# Revit family: CADS_Vent-Axia_MechEquip_Fan_SDX_InlineEC - EXTRACT
name_source: partatom
category: Mechanical Equipment
units: mm (PartAtom-declared; Revit-internal decimal feet)

## family parameters
Always vertical = Yes
Cut with Voids When Loaded = No
OmniClass Number = 23.75.00.00
OmniClass Title = Climate Control (HVAC)
Part Type = Normal
Room Calculation Point = No
Round Connector Dimension = Use Diameter
Shared = No
Work Plane-Based = No

## types (5) — shared parameters
AirflowRateRange = 0.0 L/s
AssemblyPlace = UNKNOWN
AssetType = FIXED
B = 175 mm  [stored 0.574147 ft]
DurationUnit = Year
ExteriorInsulation = No
Fitting Type = Ignore
GrossWeight = 0.00 kg
HasProtectiveEarth = No
IfcExportAs = IfcFanType
IsExtendedWarranty = No
ManufacturerAddress = Fleming Way
Crawley 
RH10 9YX
Quantity = 1
RatedCurrent = 0 A
RatedVoltage = 0 V
Status = New
WarrantyGuarantor = Vent-Axia Limited
WorkingPressure = 0.0 Pa
zero-valued in all types: CADS_Index, CADS_Usage, Default Elevation, ExpectedServiceLife, NumberOfPoles

## per-type parameters (varying)
| type | ModelReference | NominalDiameter | NominalHeight | NominalLength | NominalWidth |
| SDX125EC | INLINE 125mm FAN - EC MOTOR | 125 mm  [stored 0.410105 ft] | 245 mm  [stored 0.803806 ft] | 207 mm  [stored 0.679134 ft] | 245 mm  [stored 0.803806 ft] |
| SDX150EC | INLINE 150mm FAN - EC MOTOR | 150 mm | 344 mm  [stored 1.12861 ft] | 222 mm | 344 mm  [stored 1.12861 ft] |
| SDX200EC | INLINE 200mm FAN - EC MOTOR | 200 mm  [stored 0.656168 ft] | 345 mm  [stored 1.13189 ft] | 240 mm  [stored 0.787402 ft] | 345 mm  [stored 1.13189 ft] |
| SDX250EC | INLINE 250mm FAN - EC MOTOR | 250 mm  [stored 0.82021 ft] | 345 mm  [stored 1.13189 ft] | 245 mm  [stored 0.803806 ft] | 345 mm  [stored 1.13189 ft] |
| SDX315EC | INLINE 315mm FAN - EC MOTOR | 315 mm  [stored 1.03346 ft] | 400 mm  [stored 1.31234 ft] | 250 mm  [stored 0.82021 ft] | 400 mm  [stored 1.31234 ft] |

note: column(s) folded — value = type name in every type: ModelNumber

note: [stored X ft] marks values corroborated as IEEE doubles in the binary element streams (Revit-internal decimal feet)

## geometry (parser evidence)
native form markers: Sweep x5
no freeform markers — native parametric forms only
